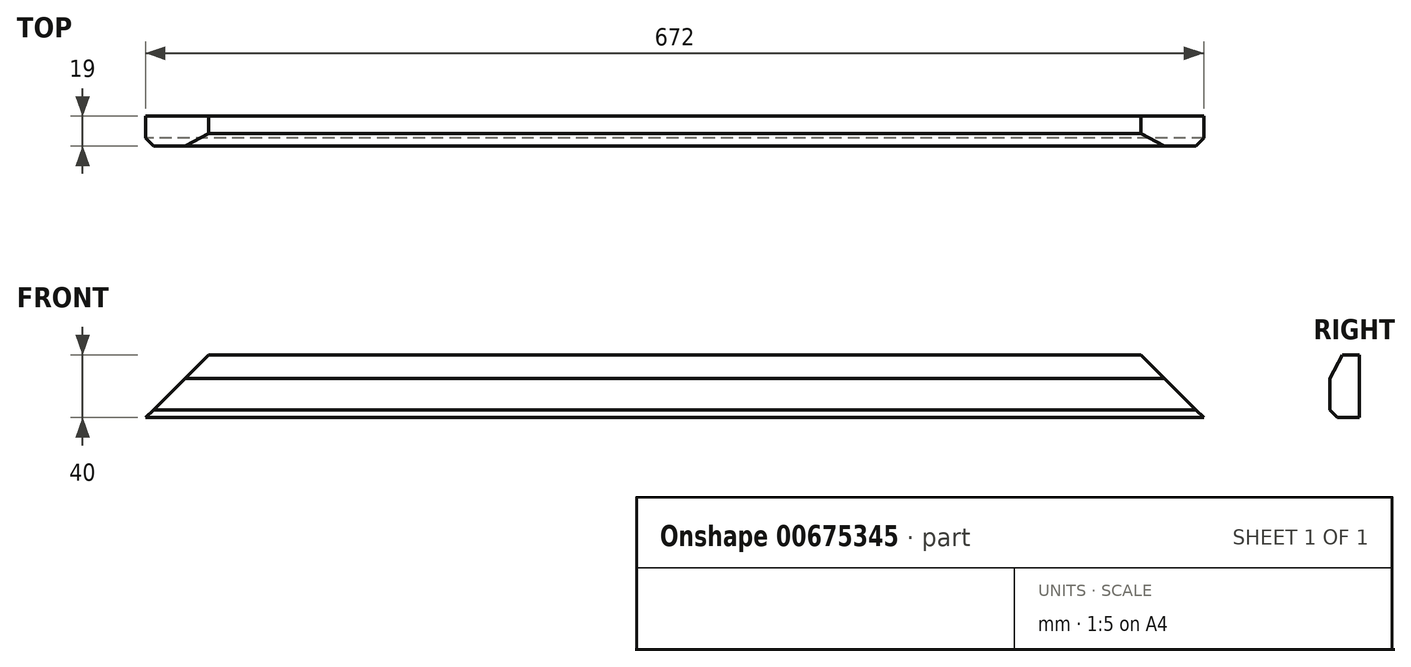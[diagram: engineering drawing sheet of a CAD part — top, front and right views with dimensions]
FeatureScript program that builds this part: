
annotation { "Feature Type Name" : "Feature", "Feature Type Description" : "" }
export const myFeature = defineFeature(function(context is Context, id is Id, definition is map)
    precondition{}
    {
        {
            var Q0;
            Q0=qCreatedBy(makeId("Right.planeOp"),FACE);
            var sketch = newSketch(context, id + "F0", { "sketchPlane" : qUnion([Q0])});
            skLineSegment(sketch, "E0", {"start": v(0, 0) * mm, "end": v(0, 40) * mm});
            skLineSegment(sketch, "E1", {"start": v(0, 40) * mm, "end": v(-11, 40) * mm});
            skLineSegment(sketch, "E2", {"start": v(0, 0) * mm, "end": v(-14, 0) * mm});
            skLineSegment(sketch, "E3", {"start": v(-14, 0) * mm, "end": v(-19, 0) * mm, "construction": true});
            skLineSegment(sketch, "E4", {"start": v(-19, 0) * mm, "end": v(-19, 5) * mm, "construction": true});
            skLineSegment(sketch, "E5", {"start": v(-14, 0) * mm, "end": v(-19, 5) * mm});
            skLineSegment(sketch, "E6", {"start": v(-19, 25) * mm, "end": v(-19, 5) * mm});
            skLineSegment(sketch, "E7", {"start": v(-19, 25) * mm, "end": v(-11, 40) * mm});
            skSolve(sketch);
        }
        {
            var Q0;
            Q0 = qSketchRegion(id + "F0", true);
            extrude(context, id + "F1", {"entities" : qUnion([Q0]), "depth" : 672 * mm, "offsetDistance" : 25 * mm});
        }
        {
            var Q0;
            Q0=qCreatedBy(makeId("Front.planeOp"),FACE);
            var sketch = newSketch(context, id + "F2", { "sketchPlane" : qUnion([Q0])});
            skLineSegment(sketch, "E8", {"start": v(0, 0) * mm, "end": v(672, 0) * mm, "construction": true});
            skLineSegment(sketch, "E9", {"start": v(336, 0) * mm, "end": v(336, 59.48) * mm, "construction": true});
            skLineSegment(sketch, "E10", {"start": v(0, 0) * mm, "end": v(0, 40) * mm});
            skLineSegment(sketch, "E11", {"start": v(0, 40) * mm, "end": v(40, 40) * mm});
            skLineSegment(sketch, "E12", {"start": v(40, 40) * mm, "end": v(0, 0) * mm});
            skLineSegment(sketch, "E13.MirrorCS", {"start": v(632, 40) * mm, "end": v(672, 0) * mm});
            skLineSegment(sketch, "E14.MirrorCS", {"start": v(672, 40) * mm, "end": v(632, 40) * mm});
            skLineSegment(sketch, "E15.MirrorCS", {"start": v(672, 0) * mm, "end": v(672, 40) * mm});
            skSolve(sketch);
        }
        {
            var Q0;
            Q0 = qSketchRegion(id + "F2", true);
            extrude(context, id + "F3", {"entities" : qUnion([Q0]), "operationType" : NewBodyOperationType.REMOVE, "depth" : 25 * mm, "offsetDistance" : 25 * mm});
        }
    });
